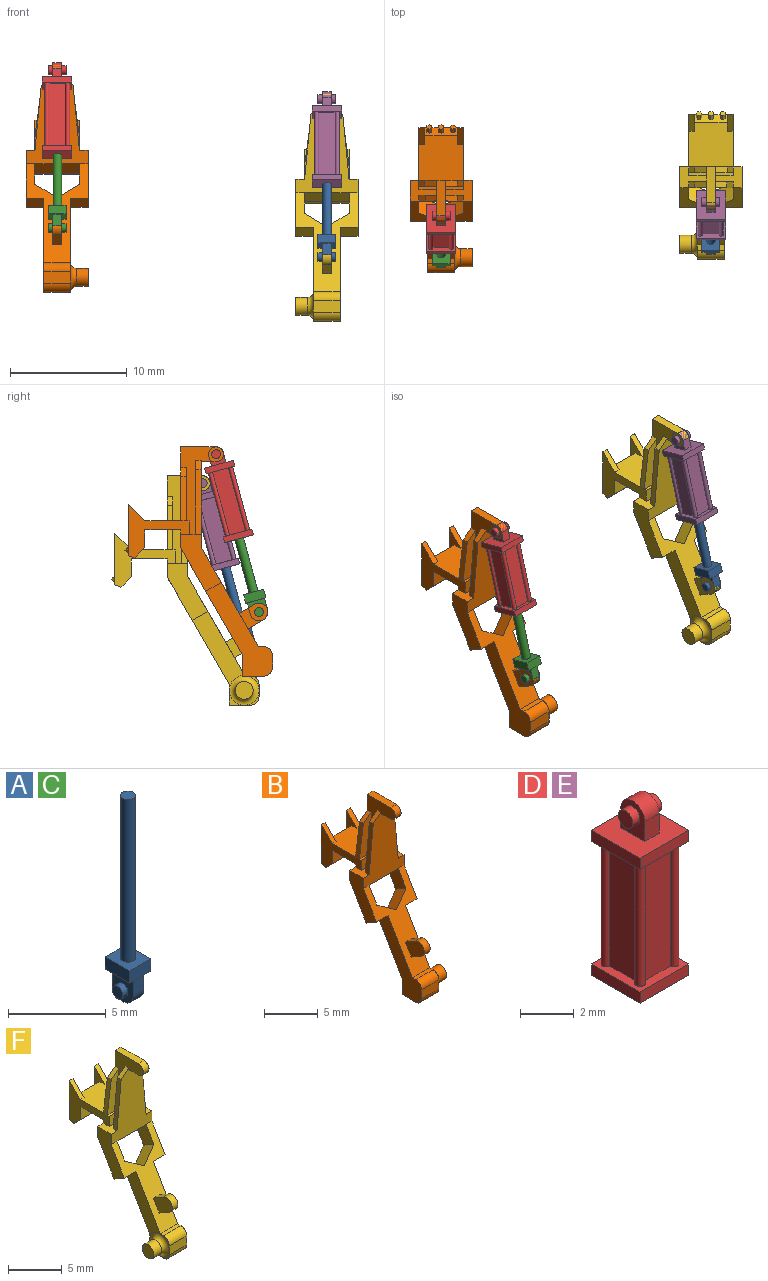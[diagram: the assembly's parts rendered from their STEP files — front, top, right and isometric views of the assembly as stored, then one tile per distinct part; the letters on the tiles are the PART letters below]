
ASSEMBLY  parts=6 mates=10
PART A: 17 faces, bbox 1.5x1.8x12.7 mm
  f0: plane 1.78x1.52mm, normal (0,0,-1), area 1.5mm2, adj f1,f2,f3,f4,f8,f9,f10,f11
  f1: plane 1.78x0.76mm, normal (-1,0,0), area 1.4mm2, adj f0,f2,f4,f5
  f2: plane 1.52x0.76mm, normal (0,-1,0), area 1.2mm2, adj f0,f1,f3,f5
  f3: plane 1.78x0.76mm, normal (1,0,0), area 1.4mm2, adj f0,f2,f4,f5
  f4: plane 1.52x0.76mm, normal (0,1,0), area 1.2mm2, adj f0,f1,f3,f5
  f5: plane 1.78x1.52mm, normal (0,0,1), area 2.3mm2, adj f1,f2,f3,f4,f6
  f6: cylinder r=0.38mm len=10.16mm, axis (0,0,-1), area 24.3mm2, adj f5,f7
  f7: plane 0.76x0.76mm, normal (0,0,1), area 0.5mm2, adj f6
  f8: plane 1.78x1.52mm, normal (-1,0,0), area 2mm2, adj f0,f9,f11,f12,f15
  f9: plane 1.02x0.76mm, normal (0,1,0), area 0.8mm2, adj f0,f8,f10,f12
  f10: plane 1.78x1.52mm, normal (1,0,0), area 2mm2, adj f0,f9,f11,f12,f14
  f11: plane 1.02x0.76mm, normal (0,-1,0), area 0.8mm2, adj f0,f8,f10,f12
  f12: cylinder r=0.76mm len=1.52mm, axis (1,0,0), area 1.8mm2, adj f8,f9,f10,f11
  f13: plane 0.76x0.76mm, normal (1,0,0), area 0.5mm2, adj f14
  f14: cylinder r=0.38mm len=0.76mm, axis (-1,0,0), area 0.9mm2, adj f10,f13
  f15: cylinder r=0.38mm len=0.76mm, axis (-1,0,0), area 0.9mm2, adj f8,f16
  f16: plane 0.76x0.76mm, normal (-1,0,0), area 0.5mm2, adj f15
PART B: 91 faces, bbox 5.3x13.1x20.1 mm
  f0: plane 1.27x1.27mm, normal (1,0,0), area 0.3mm2, adj f34,f37,f88
  f1: plane 1.27x1.27mm, normal (1,0,0), area 0.2mm2, adj f34,f36,f88,f90
  f2: plane 4.4x0.51mm, normal (0,1,0), area 2.2mm2, adj f6,f60,f61,f64
  f3: plane 2.79x2.29mm, normal (0,1,0), area 6.4mm2, adj f4,f5,f60,f62
  f4: plane 2.79x0.68mm, normal (0,0.71,0.71), area 2.2mm2, adj f3,f60,f62,f64,f65,f66,f67,f68
  f5: plane 3.81x3.81mm, normal (0,0,1), area 13.7mm2, adj f3,f6,f7,f20,f60,f61,f62,f63
  f6: plane 5.25x4.62mm, normal (1,0,0), area 8.3mm2, adj f2,f5,f10,f15,f16,f17,f18,f28
  f7: plane 5.25x4.62mm, normal (-1,0,0), area 8.3mm2, adj f5,f14,f16,f17,f18,f19,f27,f56
  f8: plane 4.57x1.52mm, normal (0,-1,0), area 5.2mm2, adj f19,f22,f56,f57
  f9: plane 4.57x1.52mm, normal (0,-1,0), area 5.2mm2, adj f10,f21,f54,f55
  f10: plane 1.52x0.25mm, normal (0,0,1), area 0.4mm2, adj f6,f9,f15,f21
  f11: plane 9.24x5.33mm, normal (0,0.87,-0.5), area 27.3mm2, adj f13,f16,f29,f30,f31,f32,f33,f37
  f12: plane 8.46x5.33mm, normal (0,-0.87,0.5), area 21.3mm2, adj f13,f24,f29,f30,f31,f32,f33,f35
  f13: plane 1.52x1.33mm, normal (0,-0.5,-0.87), area 2.3mm2, adj f11,f12,f30,f31
  f14: plane 1.52x1.14mm, normal (0,-1,0), area 1.7mm2, adj f7,f19,f22,f27
  f15: plane 1.52x1.14mm, normal (0,-1,0), area 1.7mm2, adj f6,f10,f21,f28
  f16: plane 5.33x1.52mm, normal (0,1,0), area 7.5mm2, adj f6,f7,f11,f17,f27,f28,f29,f30
  f17: plane 3.81x3.05mm, normal (0,0,-1), area 11.6mm2, adj f6,f7,f16,f18
  f18: plane 3.81x1.52mm, normal (0,-1,0), area 5.8mm2, adj f6,f7,f17,f59
  f19: plane 1.52x0.25mm, normal (0,0,1), area 0.4mm2, adj f7,f8,f14,f22
  f20: plane 6.35x3.81mm, normal (0,1,0), area 15.3mm2, adj f5,f21,f22,f25,f54,f55,f56,f57
  f21: plane 7.49x3.68mm, normal (1,0,0), area 9.1mm2, adj f9,f10,f15,f20,f23,f24,f25,f26
  f22: plane 7.49x3.68mm, normal (-1,0,0), area 9.1mm2, adj f8,f14,f19,f20,f23,f24,f25,f26
  f23: plane 1.27x0.76mm, normal (0,0,-1), area 1mm2, adj f21,f22,f24,f26
  f24: plane 7.49x5.33mm, normal (0,-1,0), area 25.5mm2, adj f12,f21,f22,f23,f27,f28,f29,f30
  f25: plane 3.05x0.76mm, normal (0,0,1), area 2.3mm2, adj f20,f21,f22,f26
  f26: cylinder r=0.64mm len=1.27mm, axis (-1,0,0), area 1.5mm2, adj f21,f22,f23,f25
  f27: plane 2.29x1.78mm, normal (0,0,1), area 2.1mm2, adj f7,f14,f16,f22,f24,f30,f48,f52
  f28: plane 2.29x1.78mm, normal (0,0,1), area 2.1mm2, adj f6,f15,f16,f21,f24,f29,f49,f51
  f29: plane 4.88x3.49mm, normal (1,0,0), area 8mm2, adj f11,f12,f16,f24,f28,f32
  f30: plane 4.88x3.49mm, normal (-1,0,0), area 8mm2, adj f11,f12,f13,f16,f24,f27
  f31: plane 8.03x5.72mm, normal (-1,0,0), area 15.5mm2, adj f11,f12,f13,f34,f35,f36,f37,f89
  f32: plane 1.52x1.33mm, normal (0,-0.5,-0.87), area 2.3mm2, adj f11,f12,f29,f33
  f33: plane 6.76x5.72mm, normal (1,0,0), area 9.8mm2, adj f11,f12,f32,f35,f36,f37,f88,f89
  f34: plane 2.29x1.78mm, normal (0,0,-1), area 4.1mm2, adj f0,f1,f31,f37,f90
  f35: plane 2.29x0.45mm, normal (0,0,1), area 1mm2, adj f12,f31,f33,f89
  f36: plane 2.29x1.02mm, normal (0,-1,0), area 2.3mm2, adj f1,f31,f33,f89,f90
  f37: plane 2.29x1.76mm, normal (0,1,0), area 4mm2, adj f0,f11,f31,f33,f34
  f38: plane 2x1.93mm, normal (-0.57,0.41,0.71), area 3.6mm2, adj f11,f12,f39,f42
  f39: plane 2.53x2.35mm, normal (-1,0,0), area 3.1mm2, adj f11,f12,f38,f40
  f40: plane 3.81x1.33mm, normal (0,-0.5,-0.87), area 5.9mm2, adj f11,f24,f39,f41
  f41: plane 2.53x2.35mm, normal (1,0,0), area 3.1mm2, adj f11,f12,f40,f42
  f42: plane 2x1.93mm, normal (0.57,0.41,0.71), area 3.6mm2, adj f11,f12,f38,f41
  f43: plane 1.32x0.76mm, normal (0,0.5,0.87), area 1.2mm2, adj f12,f44,f46,f47
  f44: cylinder r=0.76mm len=1.42mm, axis (1,0,0), area 1.8mm2, adj f43,f45,f46,f47
  f45: plane 1.32x0.76mm, normal (0,-0.5,-0.87), area 1.2mm2, adj f12,f44,f46,f47
  f46: plane 2.46x2.18mm, normal (-1,0,0), area 3.2mm2, adj f12,f43,f44,f45
  f47: plane 2.46x2.18mm, normal (1,0,0), area 3.2mm2, adj f12,f43,f44,f45
  f48: plane 6.35x1.52mm, normal (0,1,0), area 7.3mm2, adj f22,f27,f52,f53
  f49: plane 6.35x1.52mm, normal (0,1,0), area 7.3mm2, adj f21,f28,f50,f51
  f50: plane 0.98x0.81mm, normal (0.63,0,0.77), area 0.6mm2, adj f21,f24,f49,f51
  f51: plane 5.54x0.54mm, normal (1,0,0.1), area 2.8mm2, adj f24,f28,f49,f50
  f52: plane 5.54x0.54mm, normal (-1,0,0.1), area 2.8mm2, adj f24,f27,f48,f53
  f53: plane 0.98x0.81mm, normal (-0.63,0,0.77), area 0.6mm2, adj f22,f24,f48,f52
  f54: plane 1.01x0.77mm, normal (0.61,0,0.8), area 0.6mm2, adj f9,f20,f21,f55
  f55: plane 3.8x0.51mm, normal (0.99,0,0.13), area 1.9mm2, adj f6,f9,f20,f54
  f56: plane 3.8x0.51mm, normal (-0.99,0,0.13), area 1.9mm2, adj f7,f8,f20,f57
  f57: plane 1.01x0.77mm, normal (-0.61,0,0.8), area 0.6mm2, adj f8,f20,f22,f56
  f58: plane 4.4x0.51mm, normal (0,1,0), area 2.2mm2, adj f7,f62,f63,f64
  f59: plane 3.81x0.9mm, normal (0,-0.71,-0.71), area 4.8mm2, adj f6,f7,f18,f64
  f60: plane 4.4x1.44mm, normal (-1,0,0), area 2.8mm2, adj f2,f3,f4,f5,f61
  f61: plane 1.44x1.44mm, normal (0,-0.71,0.71), area 1mm2, adj f2,f5,f6,f60
  f62: plane 4.4x1.44mm, normal (1,0,0), area 2.8mm2, adj f3,f4,f5,f58,f63
  f63: plane 1.44x1.44mm, normal (0,-0.71,0.71), area 1mm2, adj f5,f7,f58,f62
  f64: plane 3.81x0.54mm, normal (0,0.38,-0.92), area 2.2mm2, adj f2,f4,f6,f7,f58,f59
  f65: plane 0.51x0.51mm, normal (-0.87,-0.35,0.35), area 0.1mm2, adj f4,f66,f70,f71
  f66: plane 0.36x0.36mm, normal (0,-0.71,0.71), area 0.1mm2, adj f4,f65,f67,f71
  f67: plane 0.51x0.51mm, normal (0.87,-0.35,0.35), area 0.1mm2, adj f4,f66,f68,f71
  f68: plane 0.51x0.51mm, normal (0.87,0.35,-0.35), area 0.1mm2, adj f4,f67,f69,f71
  f69: plane 0.36x0.36mm, normal (0,0.71,-0.71), area 0.1mm2, adj f4,f68,f70,f71
  f70: plane 0.51x0.51mm, normal (-0.87,0.35,-0.35), area 0.1mm2, adj f4,f65,f69,f71
  f71: plane 0.51x0.31mm, normal (0,0.71,0.71), area 0.2mm2, adj f65,f66,f67,f68,f69,f70
  f72: plane 0.45x0.45mm, normal (-0.5,0.61,-0.61), area 0.1mm2, adj f4,f73,f77,f78
  f73: plane 0.54x0.54mm, normal (-1,0,0), area 0.1mm2, adj f4,f72,f74,f78
  f74: plane 0.45x0.45mm, normal (-0.5,-0.61,0.61), area 0.1mm2, adj f4,f73,f75,f78
  f75: plane 0.45x0.45mm, normal (0.5,-0.61,0.61), area 0.1mm2, adj f4,f74,f76,f78
  f76: plane 0.54x0.54mm, normal (1,0,0), area 0.1mm2, adj f4,f75,f77,f78
  f77: plane 0.45x0.45mm, normal (0.5,0.61,-0.61), area 0.1mm2, adj f4,f72,f76,f78
  f78: plane 0.44x0.36mm, normal (0,0.71,0.71), area 0.2mm2, adj f72,f73,f74,f75,f76,f77
  f79: plane 0.45x0.45mm, normal (-0.5,0.61,-0.61), area 0.1mm2, adj f4,f80,f84,f85
  f80: plane 0.54x0.54mm, normal (-1,0,0), area 0.1mm2, adj f4,f79,f81,f85
  f81: plane 0.45x0.45mm, normal (-0.5,-0.61,0.61), area 0.1mm2, adj f4,f80,f82,f85
  f82: plane 0.45x0.45mm, normal (0.5,-0.61,0.61), area 0.1mm2, adj f4,f81,f83,f85
  f83: plane 0.54x0.54mm, normal (1,0,0), area 0.1mm2, adj f4,f82,f84,f85
  f84: plane 0.45x0.45mm, normal (0.5,0.61,-0.61), area 0.1mm2, adj f4,f79,f83,f85
  f85: plane 0.44x0.36mm, normal (0,0.71,0.71), area 0.2mm2, adj f79,f80,f81,f82,f83,f84
  f86: cylinder r=0.76mm len=1.52mm, axis (-1,0,0), area 4.9mm2, adj f87,f88
  f87: plane 1.52x1.52mm, normal (1,0,0), area 1.8mm2, adj f86
  f88: torus R=1.27mm, axis (1,0,0), area 4.7mm2, adj f0,f1,f33,f86
  f89: cylinder r=0.76mm len=2.29mm, axis (1,0,0), area 2.7mm2, adj f31,f33,f35,f36
  f90: cylinder r=0.76mm len=2.29mm, axis (1,0,0), area 2.7mm2, adj f1,f31,f34,f36
PART C: same geometry as A
PART D: 31 faces, bbox 2.5x2.5x8.1 mm
  f0: plane 2.54x0.51mm, normal (1,0,0), area 1.3mm2, adj f1,f3,f4,f5
  f1: plane 2.54x0.51mm, normal (0,1,0), area 1.3mm2, adj f0,f2,f4,f5
  f2: plane 2.54x0.51mm, normal (-1,0,0), area 1.3mm2, adj f1,f3,f4,f5
  f3: plane 2.54x0.51mm, normal (0,-1,0), area 1.3mm2, adj f0,f2,f4,f5
  f4: plane 2.54x2.54mm, normal (0,0,1), area 2.9mm2, adj f0,f1,f2,f3,f6,f7,f8,f9
  f5: plane 2.54x2.54mm, normal (0,0,-1), area 6mm2, adj f0,f1,f2,f3,f25
  f6: plane 5.59x1.4mm, normal (0,1,0), area 7.8mm2, adj f4,f12,f13,f14
  f7: plane 5.59x1.4mm, normal (-1,0,0), area 7.8mm2, adj f4,f10,f13,f14
  f8: plane 5.59x1.4mm, normal (1,0,0), area 7.8mm2, adj f4,f11,f12,f14
  f9: plane 5.59x1.4mm, normal (0,-1,0), area 7.8mm2, adj f4,f10,f11,f14
  f10: cylinder r=0.19mm len=5.59mm, axis (0,0,-1), area 5mm2, adj f4,f7,f9,f14
  f11: cylinder r=0.19mm len=5.59mm, axis (0,0,-1), area 5mm2, adj f4,f8,f9,f14
  f12: cylinder r=0.19mm len=5.59mm, axis (0,0,-1), area 5mm2, adj f4,f6,f8,f14
  f13: cylinder r=0.19mm len=5.59mm, axis (0,0,-1), area 5mm2, adj f4,f6,f7,f14
  f14: plane 2.54x2.54mm, normal (0,0,-1), area 2.9mm2, adj f6,f7,f8,f9,f10,f11,f12,f13
  f15: plane 2.54x0.51mm, normal (1,0,0), area 1.3mm2, adj f14,f16,f18,f19
  f16: plane 2.54x0.51mm, normal (0,1,0), area 1.3mm2, adj f14,f15,f17,f19
  f17: plane 2.54x0.51mm, normal (-1,0,0), area 1.3mm2, adj f14,f16,f18,f19
  f18: plane 2.54x0.51mm, normal (0,-1,0), area 1.3mm2, adj f14,f15,f17,f19
  f19: plane 2.54x2.54mm, normal (0,0,1), area 5.5mm2, adj f15,f16,f17,f18,f20,f21,f22,f23
  f20: plane 1.52x1.27mm, normal (-1,0,0), area 1.3mm2, adj f19,f21,f23,f24,f29
  f21: plane 0.89x0.76mm, normal (0,-1,0), area 0.7mm2, adj f19,f20,f22,f24
  f22: plane 1.52x1.27mm, normal (1,0,0), area 1.3mm2, adj f19,f21,f23,f24,f28
  f23: plane 0.89x0.76mm, normal (0,1,0), area 0.7mm2, adj f19,f20,f22,f24
  f24: cylinder r=0.64mm len=1.27mm, axis (1,0,0), area 1.5mm2, adj f20,f21,f22,f23
  f25: cylinder r=0.38mm len=0.76mm, axis (0,0,-1), area 0.6mm2, adj f5,f26
  f26: plane 0.76x0.76mm, normal (0,0,-1), area 0.5mm2, adj f25
  f27: plane 0.76x0.76mm, normal (1,0,0), area 0.5mm2, adj f28
  f28: cylinder r=0.38mm len=0.76mm, axis (-1,0,0), area 0.9mm2, adj f22,f27
  f29: cylinder r=0.38mm len=0.76mm, axis (-1,0,0), area 0.9mm2, adj f20,f30
  f30: plane 0.76x0.76mm, normal (-1,0,0), area 0.5mm2, adj f29
PART E: same geometry as D
PART F: 91 faces, bbox 5.3x13.1x20.1 mm
  f0: plane 1.27x1.27mm, normal (-1,0,0), area 0.3mm2, adj f34,f37,f88
  f1: plane 1.27x1.27mm, normal (-1,0,0), area 0.2mm2, adj f34,f36,f88,f90
  f2: plane 4.4x0.51mm, normal (0,1,0), area 2.2mm2, adj f6,f60,f61,f64
  f3: plane 2.79x2.29mm, normal (0,1,0), area 6.4mm2, adj f4,f5,f60,f62
  f4: plane 2.79x0.68mm, normal (0,0.71,0.71), area 2.2mm2, adj f3,f60,f62,f64,f65,f66,f67,f68
  f5: plane 3.81x3.81mm, normal (0,0,1), area 13.7mm2, adj f3,f6,f7,f20,f60,f61,f62,f63
  f6: plane 5.25x4.62mm, normal (-1,0,0), area 8.3mm2, adj f2,f5,f10,f15,f16,f17,f18,f28
  f7: plane 5.25x4.62mm, normal (1,0,0), area 8.3mm2, adj f5,f14,f16,f17,f18,f19,f27,f56
  f8: plane 4.57x1.52mm, normal (0,-1,0), area 5.2mm2, adj f19,f22,f56,f57
  f9: plane 4.57x1.52mm, normal (0,-1,0), area 5.2mm2, adj f10,f21,f54,f55
  f10: plane 1.52x0.25mm, normal (0,0,1), area 0.4mm2, adj f6,f9,f15,f21
  f11: plane 9.24x5.33mm, normal (0,0.87,-0.5), area 27.3mm2, adj f13,f16,f29,f30,f31,f32,f33,f37
  f12: plane 8.46x5.33mm, normal (0,-0.87,0.5), area 21.3mm2, adj f13,f24,f29,f30,f31,f32,f33,f35
  f13: plane 1.52x1.33mm, normal (0,-0.5,-0.87), area 2.3mm2, adj f11,f12,f30,f31
  f14: plane 1.52x1.14mm, normal (0,-1,0), area 1.7mm2, adj f7,f19,f22,f27
  f15: plane 1.52x1.14mm, normal (0,-1,0), area 1.7mm2, adj f6,f10,f21,f28
  f16: plane 5.33x1.52mm, normal (0,1,0), area 7.5mm2, adj f6,f7,f11,f17,f27,f28,f29,f30
  f17: plane 3.81x3.05mm, normal (0,0,-1), area 11.6mm2, adj f6,f7,f16,f18
  f18: plane 3.81x1.52mm, normal (0,-1,0), area 5.8mm2, adj f6,f7,f17,f59
  f19: plane 1.52x0.25mm, normal (0,0,1), area 0.4mm2, adj f7,f8,f14,f22
  f20: plane 6.35x3.81mm, normal (0,1,0), area 15.3mm2, adj f5,f21,f22,f25,f54,f55,f56,f57
  f21: plane 7.49x3.68mm, normal (-1,0,0), area 9.1mm2, adj f9,f10,f15,f20,f23,f24,f25,f26
  f22: plane 7.49x3.68mm, normal (1,0,0), area 9.1mm2, adj f8,f14,f19,f20,f23,f24,f25,f26
  f23: plane 1.27x0.76mm, normal (0,0,-1), area 1mm2, adj f21,f22,f24,f26
  f24: plane 7.49x5.33mm, normal (0,-1,0), area 25.5mm2, adj f12,f21,f22,f23,f27,f28,f29,f30
  f25: plane 3.05x0.76mm, normal (0,0,1), area 2.3mm2, adj f20,f21,f22,f26
  f26: cylinder r=0.64mm len=1.27mm, axis (1,0,0), area 1.5mm2, adj f21,f22,f23,f25
  f27: plane 2.29x1.78mm, normal (0,0,1), area 2.1mm2, adj f7,f14,f16,f22,f24,f30,f48,f52
  f28: plane 2.29x1.78mm, normal (0,0,1), area 2.1mm2, adj f6,f15,f16,f21,f24,f29,f49,f51
  f29: plane 4.88x3.49mm, normal (-1,0,0), area 8mm2, adj f11,f12,f16,f24,f28,f32
  f30: plane 4.88x3.49mm, normal (1,0,0), area 8mm2, adj f11,f12,f13,f16,f24,f27
  f31: plane 8.03x5.72mm, normal (1,0,0), area 15.5mm2, adj f11,f12,f13,f34,f35,f36,f37,f89
  f32: plane 1.52x1.33mm, normal (0,-0.5,-0.87), area 2.3mm2, adj f11,f12,f29,f33
  f33: plane 6.76x5.72mm, normal (-1,0,0), area 9.8mm2, adj f11,f12,f32,f35,f36,f37,f88,f89
  f34: plane 2.29x1.78mm, normal (0,0,-1), area 4.1mm2, adj f0,f1,f31,f37,f90
  f35: plane 2.29x0.45mm, normal (0,0,1), area 1mm2, adj f12,f31,f33,f89
  f36: plane 2.29x1.02mm, normal (0,-1,0), area 2.3mm2, adj f1,f31,f33,f89,f90
  f37: plane 2.29x1.76mm, normal (0,1,0), area 4mm2, adj f0,f11,f31,f33,f34
  f38: plane 2x1.93mm, normal (0.57,0.41,0.71), area 3.6mm2, adj f11,f12,f39,f42
  f39: plane 2.53x2.35mm, normal (1,0,0), area 3.1mm2, adj f11,f12,f38,f40
  f40: plane 3.81x1.33mm, normal (0,-0.5,-0.87), area 5.9mm2, adj f11,f24,f39,f41
  f41: plane 2.53x2.35mm, normal (-1,0,0), area 3.1mm2, adj f11,f12,f40,f42
  f42: plane 2x1.93mm, normal (-0.57,0.41,0.71), area 3.6mm2, adj f11,f12,f38,f41
  f43: plane 1.32x0.76mm, normal (0,0.5,0.87), area 1.2mm2, adj f12,f44,f46,f47
  f44: cylinder r=0.76mm len=1.42mm, axis (-1,0,0), area 1.8mm2, adj f43,f45,f46,f47
  f45: plane 1.32x0.76mm, normal (0,-0.5,-0.87), area 1.2mm2, adj f12,f44,f46,f47
  f46: plane 2.46x2.18mm, normal (1,0,0), area 3.2mm2, adj f12,f43,f44,f45
  f47: plane 2.46x2.18mm, normal (-1,0,0), area 3.2mm2, adj f12,f43,f44,f45
  f48: plane 6.35x1.52mm, normal (0,1,0), area 7.3mm2, adj f22,f27,f52,f53
  f49: plane 6.35x1.52mm, normal (0,1,0), area 7.3mm2, adj f21,f28,f50,f51
  f50: plane 0.98x0.81mm, normal (-0.63,0,0.77), area 0.6mm2, adj f21,f24,f49,f51
  f51: plane 5.54x0.54mm, normal (-1,0,0.1), area 2.8mm2, adj f24,f28,f49,f50
  f52: plane 5.54x0.54mm, normal (1,0,0.1), area 2.8mm2, adj f24,f27,f48,f53
  f53: plane 0.98x0.81mm, normal (0.63,0,0.77), area 0.6mm2, adj f22,f24,f48,f52
  f54: plane 1.01x0.77mm, normal (-0.61,0,0.8), area 0.6mm2, adj f9,f20,f21,f55
  f55: plane 3.8x0.51mm, normal (-0.99,0,0.13), area 1.9mm2, adj f6,f9,f20,f54
  f56: plane 3.8x0.51mm, normal (0.99,0,0.13), area 1.9mm2, adj f7,f8,f20,f57
  f57: plane 1.01x0.77mm, normal (0.61,0,0.8), area 0.6mm2, adj f8,f20,f22,f56
  f58: plane 4.4x0.51mm, normal (0,1,0), area 2.2mm2, adj f7,f62,f63,f64
  f59: plane 3.81x0.9mm, normal (0,-0.71,-0.71), area 4.8mm2, adj f6,f7,f18,f64
  f60: plane 4.4x1.44mm, normal (1,0,0), area 2.8mm2, adj f2,f3,f4,f5,f61
  f61: plane 1.44x1.44mm, normal (0,-0.71,0.71), area 1mm2, adj f2,f5,f6,f60
  f62: plane 4.4x1.44mm, normal (-1,0,0), area 2.8mm2, adj f3,f4,f5,f58,f63
  f63: plane 1.44x1.44mm, normal (0,-0.71,0.71), area 1mm2, adj f5,f7,f58,f62
  f64: plane 3.81x0.54mm, normal (0,0.38,-0.92), area 2.2mm2, adj f2,f4,f6,f7,f58,f59
  f65: plane 0.51x0.51mm, normal (0.87,-0.35,0.35), area 0.1mm2, adj f4,f66,f70,f71
  f66: plane 0.36x0.36mm, normal (0,-0.71,0.71), area 0.1mm2, adj f4,f65,f67,f71
  f67: plane 0.51x0.51mm, normal (-0.87,-0.35,0.35), area 0.1mm2, adj f4,f66,f68,f71
  f68: plane 0.51x0.51mm, normal (-0.87,0.35,-0.35), area 0.1mm2, adj f4,f67,f69,f71
  f69: plane 0.36x0.36mm, normal (0,0.71,-0.71), area 0.1mm2, adj f4,f68,f70,f71
  f70: plane 0.51x0.51mm, normal (0.87,0.35,-0.35), area 0.1mm2, adj f4,f65,f69,f71
  f71: plane 0.51x0.31mm, normal (0,0.71,0.71), area 0.2mm2, adj f65,f66,f67,f68,f69,f70
  f72: plane 0.45x0.45mm, normal (0.5,0.61,-0.61), area 0.1mm2, adj f4,f73,f77,f78
  f73: plane 0.54x0.54mm, normal (1,0,0), area 0.1mm2, adj f4,f72,f74,f78
  f74: plane 0.45x0.45mm, normal (0.5,-0.61,0.61), area 0.1mm2, adj f4,f73,f75,f78
  f75: plane 0.45x0.45mm, normal (-0.5,-0.61,0.61), area 0.1mm2, adj f4,f74,f76,f78
  f76: plane 0.54x0.54mm, normal (-1,0,0), area 0.1mm2, adj f4,f75,f77,f78
  f77: plane 0.45x0.45mm, normal (-0.5,0.61,-0.61), area 0.1mm2, adj f4,f72,f76,f78
  f78: plane 0.44x0.36mm, normal (0,0.71,0.71), area 0.2mm2, adj f72,f73,f74,f75,f76,f77
  f79: plane 0.45x0.45mm, normal (0.5,0.61,-0.61), area 0.1mm2, adj f4,f80,f84,f85
  f80: plane 0.54x0.54mm, normal (1,0,0), area 0.1mm2, adj f4,f79,f81,f85
  f81: plane 0.45x0.45mm, normal (0.5,-0.61,0.61), area 0.1mm2, adj f4,f80,f82,f85
  f82: plane 0.45x0.45mm, normal (-0.5,-0.61,0.61), area 0.1mm2, adj f4,f81,f83,f85
  f83: plane 0.54x0.54mm, normal (-1,0,0), area 0.1mm2, adj f4,f82,f84,f85
  f84: plane 0.45x0.45mm, normal (-0.5,0.61,-0.61), area 0.1mm2, adj f4,f79,f83,f85
  f85: plane 0.44x0.36mm, normal (0,0.71,0.71), area 0.2mm2, adj f79,f80,f81,f82,f83,f84
  f86: cylinder r=0.76mm len=1.52mm, axis (1,0,0), area 4.9mm2, adj f87,f88
  f87: plane 1.52x1.52mm, normal (-1,0,0), area 1.8mm2, adj f86
  f88: torus R=1.27mm, axis (-1,0,0), area 4.7mm2, adj f0,f1,f33,f86
  f89: cylinder r=0.76mm len=2.29mm, axis (-1,0,0), area 2.7mm2, adj f31,f33,f35,f36
  f90: cylinder r=0.76mm len=2.29mm, axis (-1,0,0), area 2.7mm2, adj f1,f31,f34,f36
PLACE A rot(axis=(-1,0,0),15.2deg) t=(36.42,-7.94,-2.07)mm
PLACE B t=(-14.66,0.81,4)mm fixed
PLACE C rot(axis=(-1,0,0),15.2deg) t=(13.34,-9.1,0.42)mm
PLACE D rot(axis=(-1,0,0),15.2deg) t=(-13.39,-5.42,5.11)mm
PLACE E rot(axis=(-1,0,0),15.2deg) t=(9.69,-4.27,2.62)mm
PLACE F t=(41.95,1.97,1.52)mm fixed
MATE planar E.f22 <-> F.f22  axis (1,0,0) through (8.8,-1.31,8.66)mm
MATE planar C.f8 <-> B.f46  axis (-1,0,0) through (-15.04,-6.5,-0.81)mm
MATE planar B.f26 <-> D.f22  axis (1,0,0) through (-14.28,-2.23,12)mm
MATE cylindrical E.f24 <-> F.f26  axis (1,0,0) through (8.42,-1.08,9.52)mm
MATE cylindrical A.f12 <-> F.f44  axis (1,0,0) through (8.42,-4.75,-3.99)mm
MATE planar F.f46 <-> A.f10  axis (1,0,0) through (8.8,-4.36,-4.22)mm
MATE cylindrical D.f24 <-> B.f26  axis (1,0,0) through (-14.66,-2.23,12)mm
MATE cylindrical E.f25 <-> A.f6  axis (0,-0.26,-0.97) through (8.42,-3.01,2.41)mm
MATE cylindrical C.f6 <-> D.f25  axis (0,-0.26,-0.97) through (-14.66,-4.1,5.11)mm
MATE cylindrical C.f12 <-> B.f44  axis (1,0,0) through (-14.66,-5.9,-1.5)mm
